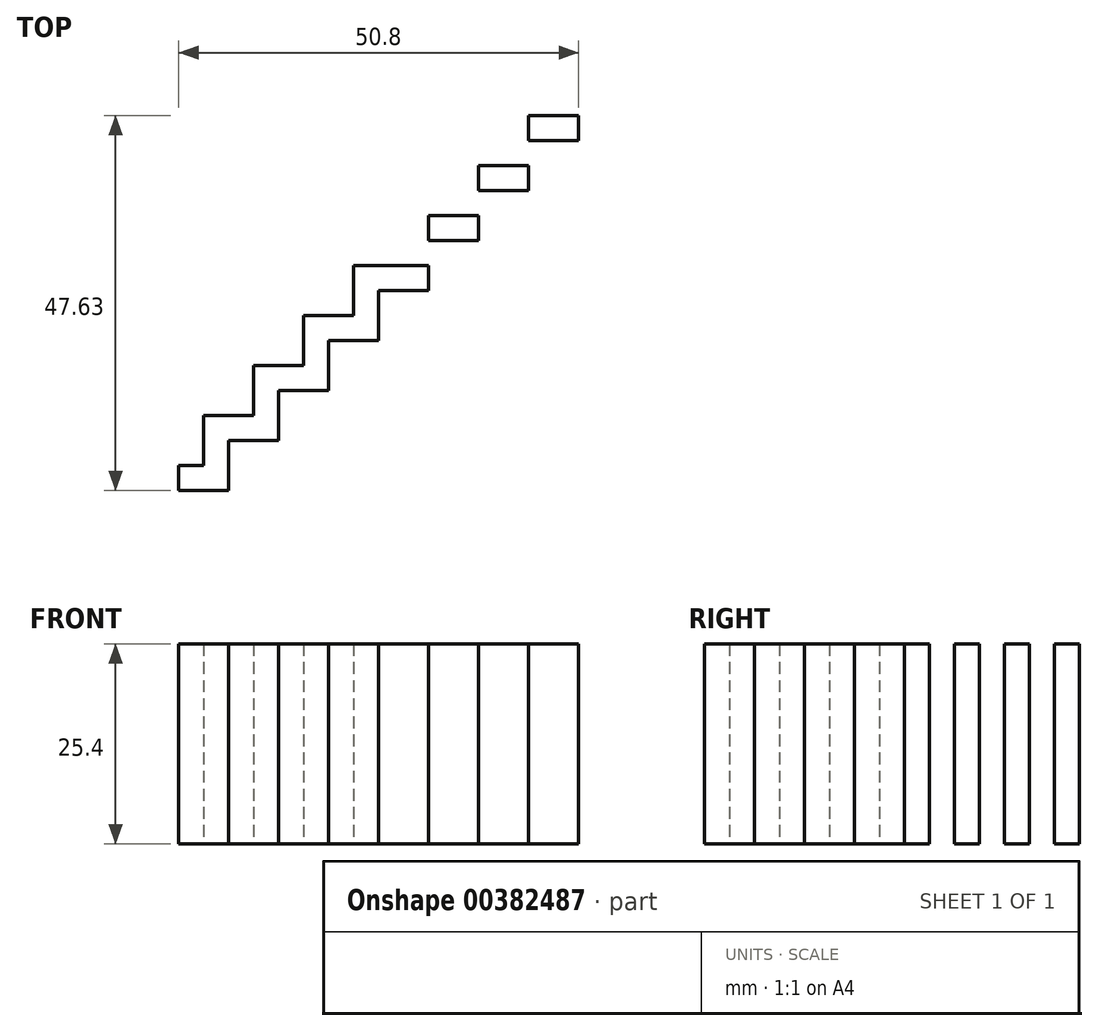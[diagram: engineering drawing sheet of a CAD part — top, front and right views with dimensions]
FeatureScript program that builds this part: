
annotation { "Feature Type Name" : "Feature", "Feature Type Description" : "" }
export const myFeature = defineFeature(function(context is Context, id is Id, definition is map)
    precondition{}
    {
        {
            var Q0;
            Q0=qCreatedBy(makeId("Top.planeOp"),FACE);
            var sketch = newSketch(context, id + "F0", { "sketchPlane" : qUnion([Q0])});
            skLineSegment(sketch, "E0.bottom", {"start": v(0, 0) * mm, "end": v(6.35, 0) * mm});
            skLineSegment(sketch, "E0.top", {"start": v(0, 3.18) * mm, "end": v(6.35, 3.18) * mm});
            skLineSegment(sketch, "E0.left", {"start": v(0, 0) * mm, "end": v(0, 3.18) * mm});
            skLineSegment(sketch, "E0.right", {"start": v(6.35, 0) * mm, "end": v(6.35, 3.18) * mm});
            skLineSegment(sketch, "E1.bottom", {"start": v(6.35, 3.18) * mm, "end": v(3.18, 3.18) * mm});
            skLineSegment(sketch, "E1.top", {"start": v(6.35, 9.53) * mm, "end": v(3.17, 9.53) * mm});
            skLineSegment(sketch, "E1.left", {"start": v(6.35, 3.18) * mm, "end": v(6.35, 9.53) * mm});
            skLineSegment(sketch, "E1.right", {"start": v(3.18, 3.18) * mm, "end": v(3.17, 9.53) * mm});
            skLineSegment(sketch, "E2.bottom", {"start": v(6.35, 9.53) * mm, "end": v(12.7, 9.53) * mm});
            skLineSegment(sketch, "E2.top", {"start": v(6.35, 6.35) * mm, "end": v(12.7, 6.35) * mm});
            skLineSegment(sketch, "E2.left", {"start": v(6.35, 9.53) * mm, "end": v(6.35, 6.35) * mm});
            skLineSegment(sketch, "E2.right", {"start": v(12.7, 9.53) * mm, "end": v(12.7, 6.35) * mm});
            skLineSegment(sketch, "E3.bottom", {"start": v(12.7, 9.53) * mm, "end": v(9.52, 9.53) * mm});
            skLineSegment(sketch, "E3.top", {"start": v(12.7, 15.87) * mm, "end": v(9.52, 15.87) * mm});
            skLineSegment(sketch, "E3.left", {"start": v(12.7, 9.53) * mm, "end": v(12.7, 15.87) * mm});
            skLineSegment(sketch, "E3.right", {"start": v(9.53, 9.53) * mm, "end": v(9.52, 15.88) * mm});
            skLineSegment(sketch, "E4.bottom", {"start": v(12.7, 15.87) * mm, "end": v(19.05, 15.87) * mm});
            skLineSegment(sketch, "E4.top", {"start": v(12.7, 12.7) * mm, "end": v(19.05, 12.7) * mm});
            skLineSegment(sketch, "E4.left", {"start": v(12.7, 15.87) * mm, "end": v(12.7, 12.7) * mm});
            skLineSegment(sketch, "E4.right", {"start": v(19.05, 15.87) * mm, "end": v(19.05, 12.7) * mm});
            skLineSegment(sketch, "E5.bottom", {"start": v(19.05, 15.87) * mm, "end": v(15.88, 15.87) * mm});
            skLineSegment(sketch, "E5.top", {"start": v(19.05, 22.23) * mm, "end": v(15.88, 22.23) * mm});
            skLineSegment(sketch, "E5.left", {"start": v(19.05, 15.87) * mm, "end": v(19.05, 22.22) * mm});
            skLineSegment(sketch, "E5.right", {"start": v(15.88, 15.87) * mm, "end": v(15.88, 22.22) * mm});
            skLineSegment(sketch, "E6.bottom", {"start": v(19.05, 22.23) * mm, "end": v(25.4, 22.23) * mm});
            skLineSegment(sketch, "E6.top", {"start": v(19.05, 19.05) * mm, "end": v(25.4, 19.05) * mm});
            skLineSegment(sketch, "E6.left", {"start": v(19.05, 22.22) * mm, "end": v(19.05, 19.05) * mm});
            skLineSegment(sketch, "E6.right", {"start": v(25.4, 22.23) * mm, "end": v(25.4, 19.05) * mm});
            skLineSegment(sketch, "E7.bottom", {"start": v(25.4, 22.23) * mm, "end": v(22.23, 22.23) * mm});
            skLineSegment(sketch, "E7.top", {"start": v(25.4, 28.57) * mm, "end": v(22.23, 28.57) * mm});
            skLineSegment(sketch, "E7.left", {"start": v(25.4, 22.23) * mm, "end": v(25.4, 28.58) * mm});
            skLineSegment(sketch, "E7.right", {"start": v(22.23, 22.23) * mm, "end": v(22.23, 28.58) * mm});
            skLineSegment(sketch, "E8.bottom", {"start": v(0, 0) * mm, "end": v(0, 0) * mm});
            skLineSegment(sketch, "E8.top", {"start": v(0, 3.18) * mm, "end": v(0, 3.18) * mm});
            skLineSegment(sketch, "E9.bottom", {"start": v(0, 3.18) * mm, "end": v(-3.18, 3.18) * mm});
            skLineSegment(sketch, "E9.top", {"start": v(0, -3.17) * mm, "end": v(-3.17, -3.17) * mm});
            skLineSegment(sketch, "E9.left", {"start": v(0, 3.18) * mm, "end": v(0, -3.17) * mm});
            skLineSegment(sketch, "E9.right", {"start": v(-3.18, 3.18) * mm, "end": v(-3.17, -3.17) * mm});
            skLineSegment(sketch, "E10.bottom", {"start": v(0, -3.17) * mm, "end": v(-6.35, -3.17) * mm});
            skLineSegment(sketch, "E10.top", {"start": v(0, -6.35) * mm, "end": v(-6.35, -6.35) * mm});
            skLineSegment(sketch, "E10.left", {"start": v(0, -3.17) * mm, "end": v(0, -6.35) * mm});
            skLineSegment(sketch, "E10.right", {"start": v(-6.35, -3.17) * mm, "end": v(-6.35, -6.35) * mm});
            skLineSegment(sketch, "E11.bottom", {"start": v(-6.35, -3.17) * mm, "end": v(-9.53, -3.18) * mm});
            skLineSegment(sketch, "E11.top", {"start": v(-6.35, -9.52) * mm, "end": v(-9.53, -9.52) * mm});
            skLineSegment(sketch, "E11.left", {"start": v(-6.35, -3.17) * mm, "end": v(-6.35, -9.52) * mm});
            skLineSegment(sketch, "E11.right", {"start": v(-9.53, -3.17) * mm, "end": v(-9.52, -9.52) * mm});
            skLineSegment(sketch, "E12.bottom", {"start": v(-6.35, -9.52) * mm, "end": v(-12.7, -9.52) * mm});
            skLineSegment(sketch, "E12.top", {"start": v(-6.35, -12.7) * mm, "end": v(-12.7, -12.7) * mm});
            skLineSegment(sketch, "E12.left", {"start": v(-6.35, -9.52) * mm, "end": v(-6.35, -12.7) * mm});
            skLineSegment(sketch, "E12.right", {"start": v(-12.7, -9.52) * mm, "end": v(-12.7, -12.7) * mm});
            skLineSegment(sketch, "E13.bottom", {"start": v(-12.7, -9.52) * mm, "end": v(-15.88, -9.53) * mm});
            skLineSegment(sketch, "E13.top", {"start": v(-12.7, -15.88) * mm, "end": v(-15.88, -15.88) * mm});
            skLineSegment(sketch, "E13.left", {"start": v(-12.7, -9.52) * mm, "end": v(-12.7, -15.88) * mm});
            skLineSegment(sketch, "E13.right", {"start": v(-15.88, -9.52) * mm, "end": v(-15.88, -15.88) * mm});
            skLineSegment(sketch, "E14.bottom", {"start": v(-12.7, -15.88) * mm, "end": v(-19.05, -15.88) * mm});
            skLineSegment(sketch, "E14.top", {"start": v(-12.7, -19.05) * mm, "end": v(-19.05, -19.05) * mm});
            skLineSegment(sketch, "E14.left", {"start": v(-12.7, -15.88) * mm, "end": v(-12.7, -19.05) * mm});
            skLineSegment(sketch, "E14.right", {"start": v(-19.05, -15.88) * mm, "end": v(-19.05, -19.05) * mm});
            skLineSegment(sketch, "E15.bottom", {"start": v(-19.05, -15.88) * mm, "end": v(-22.22, -15.88) * mm});
            skLineSegment(sketch, "E15.top", {"start": v(-19.05, -22.23) * mm, "end": v(-22.22, -22.23) * mm});
            skLineSegment(sketch, "E15.left", {"start": v(-19.05, -15.88) * mm, "end": v(-19.05, -22.23) * mm});
            skLineSegment(sketch, "E15.right", {"start": v(-22.22, -15.88) * mm, "end": v(-22.22, -22.23) * mm});
            skLineSegment(sketch, "E16.bottom", {"start": v(-19.05, -22.23) * mm, "end": v(-25.4, -22.23) * mm});
            skLineSegment(sketch, "E16.top", {"start": v(-19.05, -25.4) * mm, "end": v(-25.4, -25.4) * mm});
            skLineSegment(sketch, "E16.left", {"start": v(-19.05, -22.23) * mm, "end": v(-19.05, -25.4) * mm});
            skLineSegment(sketch, "E16.right", {"start": v(-25.4, -22.23) * mm, "end": v(-25.4, -25.4) * mm});
            skSolve(sketch);
        }
        {
            var Q0;
            {var subQ5=sQuery(id+"F0.wireOp",EDGE,"E13.bottom");Q0=makeQuery(id+"F0.imprint","IMPRINT",FACE,{"disambiguationData":[TD([[makeQuery(id+"F0.imprint","IMPRINT",EDGE,{"derivedFrom":subQ5}),1.0]])]});}
            var Q1;
            {var subQ5=sQuery(id+"F0.wireOp",EDGE,"E15.bottom");Q1=makeQuery(id+"F0.imprint","IMPRINT",FACE,{"disambiguationData":[TD([[makeQuery(id+"F0.imprint","IMPRINT",EDGE,{"derivedFrom":subQ5}),1.0]])]});}
            var Q2;
            {var subQ1=sQuery(id+"F0.wireOp",EDGE,"E14.top");Q2=makeQuery(id+"F0.imprint","IMPRINT",FACE,{"disambiguationData":[TD([[makeQuery(id+"F0.imprint","IMPRINT",EDGE,{"derivedFrom":subQ1}),-1.0]])]});}
            var Q3;
            {var subQ5=sQuery(id+"F0.wireOp",EDGE,"E9.bottom");Q3=makeQuery(id+"F0.imprint","IMPRINT",FACE,{"disambiguationData":[TD([[makeQuery(id+"F0.imprint","IMPRINT",EDGE,{"derivedFrom":subQ5}),1.0]])]});}
            var Q4;
            {var subQ1=sQuery(id+"F0.wireOp",EDGE,"E10.top");Q4=makeQuery(id+"F0.imprint","IMPRINT",FACE,{"disambiguationData":[TD([[makeQuery(id+"F0.imprint","IMPRINT",EDGE,{"derivedFrom":subQ1}),-1.0]])]});}
            var Q5;
            {var subQ5=sQuery(id+"F0.wireOp",EDGE,"E11.bottom");Q5=makeQuery(id+"F0.imprint","IMPRINT",FACE,{"disambiguationData":[TD([[makeQuery(id+"F0.imprint","IMPRINT",EDGE,{"derivedFrom":subQ5}),1.0]])]});}
            var Q6;
            Q6=makeQuery(id+"F0.imprint","IMPRINT",FACE,{"disambiguationData":[TD([[makeQuery(id+"F0.imprint","IMPRINT",EDGE,{"derivedFrom":sQuery(id+"F0.wireOp",EDGE,"E6.bottom")}),-1.0]])]});
            var Q7;
            Q7=makeQuery(id+"F0.imprint","IMPRINT",FACE,{"disambiguationData":[TD([[makeQuery(id+"F0.imprint","IMPRINT",EDGE,{"derivedFrom":sQuery(id+"F0.wireOp",EDGE,"E4.bottom")}),-1.0]])]});
            var Q8;
            Q8=makeQuery(id+"F0.imprint","IMPRINT",FACE,{"disambiguationData":[TD([[makeQuery(id+"F0.imprint","IMPRINT",EDGE,{"derivedFrom":sQuery(id+"F0.wireOp",EDGE,"E5.bottom")}),-1.0]])]});
            var Q9;
            Q9=makeQuery(id+"F0.imprint","IMPRINT",FACE,{"disambiguationData":[TD([[makeQuery(id+"F0.imprint","IMPRINT",EDGE,{"derivedFrom":sQuery(id+"F0.wireOp",EDGE,"E3.bottom")}),-1.0]])]});
            var Q10;
            Q10=makeQuery(id+"F0.imprint","IMPRINT",FACE,{"disambiguationData":[TD([[makeQuery(id+"F0.imprint","IMPRINT",EDGE,{"derivedFrom":sQuery(id+"F0.wireOp",EDGE,"E2.bottom")}),-1.0]])]});
            var Q11;
            {var subQ1=sQuery(id+"F0.wireOp",EDGE,"E12.top");Q11=makeQuery(id+"F0.imprint","IMPRINT",FACE,{"disambiguationData":[TD([[makeQuery(id+"F0.imprint","IMPRINT",EDGE,{"derivedFrom":subQ1}),-1.0]])]});}
            var Q12;
            Q12=makeQuery(id+"F0.imprint","IMPRINT",FACE,{"disambiguationData":[TD([[makeQuery(id+"F0.imprint","IMPRINT",EDGE,{"derivedFrom":sQuery(id+"F0.wireOp",EDGE,"E1.bottom")}),-1.0]])]});
            var Q13;
            {var subQ1=sQuery(id+"F0.wireOp",EDGE,"E0.bottom");Q13=makeQuery(id+"F0.imprint","IMPRINT",FACE,{"disambiguationData":[TD([[makeQuery(id+"F0.imprint","IMPRINT",EDGE,{"derivedFrom":subQ1}),1.0]])]});}
            var Q14;
            Q14=makeQuery(id+"F0.imprint","IMPRINT",FACE,{"disambiguationData":[TD([[makeQuery(id+"F0.imprint","IMPRINT",EDGE,{"derivedFrom":sQuery(id+"F0.wireOp",EDGE,"E16.top")}),-1.0]])]});
            var Q15;
            Q15=makeQuery(id+"F0.imprint","IMPRINT",FACE,{"disambiguationData":[TD([[makeQuery(id+"F0.imprint","IMPRINT",EDGE,{"derivedFrom":sQuery(id+"F0.wireOp",EDGE,"E7.bottom")}),-1.0]])]});
            extrude(context, id + "F1", {"entities" : qUnion([Q0, Q1, Q2, Q3, Q4, Q5, Q6, Q7, Q8, Q9, Q10, Q11, Q12, Q13, Q14, Q15]), "depth" : 25.4 * mm});
        }
    });
